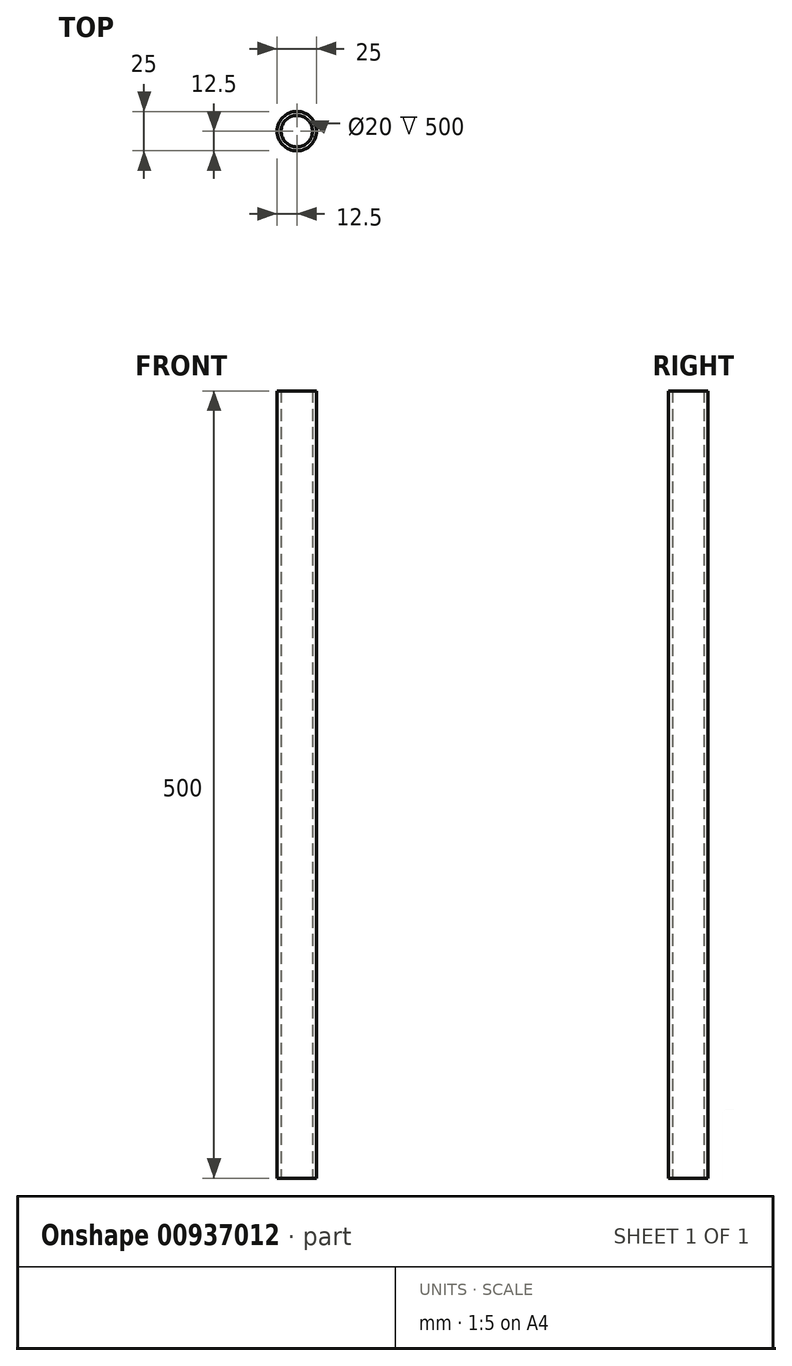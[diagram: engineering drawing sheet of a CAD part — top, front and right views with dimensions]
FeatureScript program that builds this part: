
annotation { "Feature Type Name" : "Feature", "Feature Type Description" : "" }
export const myFeature = defineFeature(function(context is Context, id is Id, definition is map)
    precondition{}
    {
        {
            var Q0;
            Q0=qCreatedBy(makeId("Top.planeOp"),FACE);
            var sketch = newSketch(context, id + "F0", { "sketchPlane" : qUnion([Q0])});
            skCircle(sketch, "E0", {"center": v(0, 0) * mm, "radius": 12.5 * mm});
            skCircle(sketch, "E1", {"center": v(0, 0) * mm, "radius": 10 * mm});
            skSolve(sketch);
        }
        {
            var Q0;
            Q0=makeQuery(id+"F0.imprint","IMPRINT",FACE,{"disambiguationData":[TD([[makeQuery(id+"F0.imprint","IMPRINT",EDGE,{"derivedFrom":sQuery(id+"F0.wireOp",EDGE,"E0")}),1.0]])]});
            extrude(context, id + "F1", {"entities" : qUnion([Q0]), "depth" : 500 * mm, "offsetDistance" : 25 * mm});
        }
    });
